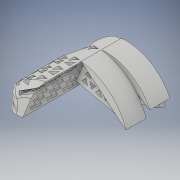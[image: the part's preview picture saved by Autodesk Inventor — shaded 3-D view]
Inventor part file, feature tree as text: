
AUTODESK INVENTOR PART (.ipt)
format: ipt  version: 2017 (Build 210142000, 142)  size: 1,097,728 bytes
history: native  units: mm
features: sketch x28, extrude x24, plane x7, fillet x6, other x3, boolean_combine x1, revolve x1, sweep x1
ambient origin geometry x8: Origin, YZ Plane, XZ Plane, XY Plane, X Axis, Y Axis, Z Axis, Center Point
bodies: Solid1 (feature_tree), Solid2 (feature_tree), Solid3 (feature_tree), Solid4 (feature_tree), Solid5 (feature_tree)
feature tree (71):
  extrude  "Extrusion1"  Depth=35.0mm
  plane  "Work Plane1"
  extrude  "Extrusion2"  Depth=33.005mm
  extrude  "Extrusion3"  TaperAngle=0.0deg  [1 undecoded]
  plane  "Work Plane2"
  extrude  "Extrusion4"  Depth=20.0mm
  other  "Work Axis1"
  extrude  "Extrusion5"  Depth=10.0mm
  sketch  "Sketch6"  dims[d12=48.556624mm d13=20.0mm d14=0.0mm]
  boolean_combine  "Combine1"
  extrude  "Extrusion6"  Depth=20.0mm TaperAngle=0.0deg
  extrude  "Extrusion7"  Depth=53.287466mm TaperAngle=0.0deg
  other  "Work Axis2"
  fillet  "Fillet1"  Radius=53.287466mm
  revolve  "Revolution1"  [1 undecoded]
  extrude  "Extrusion8"  Depth=61.358233mm
  sketch  "Sketch10"  dims[d25=7.433428mm d26=13.25mm d27=0.0mm]
  plane  "Work Plane3"
  sweep  "Sweep1"
  extrude  "Extrusion9"  TaperAngle=90.0deg  [1 undecoded]
  fillet  "Fillet2"  Radius=40.197898mm
  extrude  "Extrusion10"  Depth=15.060899mm
  extrude  "Extrusion11"  Depth=10.650813mm
  extrude  "Extrusion12"  Depth=5.3475mm
  fillet  "Fillet3"  Radius=15.0mm
  fillet  "Fillet4"  [1 undecoded]
  fillet  "Fillet5"  Radius=27.295196mm
  other  "Bend Part1"
  extrude  "Extrusion13"  Depth=5.348mm
  plane  "Work Plane4"
  extrude  "Extrusion14"  TaperAngle=0.0deg  [1 undecoded]
  fillet  "Fillet6"  Radius=13.25mm
  extrude  "Extrusion15"  Depth=10.0mm TaperAngle=0.0deg
  plane  "Work Plane5"
  extrude  "Extrusion16"  Depth=10.0mm
  extrude  "Extrusion22"  Depth=10.0mm TaperAngle=0.0deg
  extrude  "Extrusion23"  Depth=10.0mm
  extrude  "Extrusion24"  Depth=10.0mm TaperAngle=180.0deg
  extrude  "Extrusion25"  Depth=18.153275mm
  plane  "Work Plane7"
  extrude  "Extrusion26"  TaperAngle=90.0deg  [1 undecoded]
  extrude  "Extrusion27"  Depth=57.396209mm
  extrude  "Extrusion28"  Depth=2.0mm
  plane  "Work Plane8"
  extrude  "Extrusion29"  Depth=17.5mm
  sketch  "Sketch1"  dims[d0=60.0mm d1=35.0mm]
  sketch  "Sketch2"  dims[d2=60.0mm d3=33.005mm]
  sketch  "Sketch3"  dims[d4=75.0mm d5=0.0mm d6=0.0mm]
  sketch  "Sketch4"  dims[d7=35.0mm d8=20.0mm]
  sketch  "Sketch5"  dims[d9=55.0mm d10=0.0mm d11=10.0mm]
  sketch  "Sketch7"  dims[d15=90.0deg d16=20.0mm d17=0.0mm d18=53.287466mm]
  sketch  "Sketch8"  dims[d19=20.0mm d20=0.0mm d21=14.476257mm]
  sketch  "Sketch9"  dims[d22=20.0mm d23=0.0mm d24=61.358233mm]
  sketch  "Sketch11"  dims[d28=10.0mm d29=90.0deg d30=40.197898mm]
  sketch  "Sketch12"  dims[d31=90.965929mm d32=15.060899mm]
  sketch  "Sketch13"  dims[d33=0.0mm d34=0.0mm d35=10.650813mm]
  sketch  "Sketch15"  dims[d36=90.0deg d37=5.3475mm d38=15.0mm d39=45.0deg d40=27.295196mm]
  sketch  "Sketch16"  dims[d41=20.0mm d42=5.348mm]
  sketch  "Sketch18"  dims[d43=60.0mm d44=0.0mm d45=0.0mm d46=13.25mm d47=0.0mm]
  sketch  "Sketch19"  dims[d48=10.0mm d49=75.0mm d50=0.0mm]
  sketch  "Sketch20"  dims[d52=10.0mm d53=10.80569mm]
  sketch  "Sketch21"  dims[d54=10.0mm d55=0.0mm d56=4.8mm d57=0.0mm]
  sketch  "Sketch22"  dims[d58=10.0mm d59=10.0mm]
  sketch  "Sketch28"  dims[d60=10.0mm d62=2.0mm d63=180.0deg]
  sketch  "Sketch29"  dims[d64=18.153275mm d65=18.153275mm]
  sketch  "Sketch30"  dims[d66=75.0mm d67=0.0mm d68=90.0deg]
  sketch  "Sketch31"  dims[d69=75.0mm d70=57.396209mm]
  sketch  "Sketch32"  dims[d71=75.0mm d72=0.0mm d73=2.0mm]
  sketch  "Sketch33"  dims[d74=27.7545mm d75=17.5mm]
  sketch  "Sketch34"  dims[d76=5.0mm d77=0.0mm]
  sketch  "Sketch35"  dims[d78=20.0mm d79=28.8585mm d80=10.0mm d81=0.0mm d108=10.0mm d109=0.0mm d110=5.0mm d111=0.0mm d112=20.0mm d113=3.0mm d114=2.5mm d115=19.198622mm d116=10.0mm d117=0.0mm d118=20.0mm d119=3.0mm d120=13.189mm d121=20.0mm d122=3.0mm d123=11.073mm d124=10.0mm d125=5.0mm d126=0.0mm d127=0.0mm d128=5.202827mm d129=2.5mm d130=20.0mm d131=47.662mm d132=0.0mm d133=6.0mm d134=4.0mm d136=4.0mm d137=6.0mm d138=4.0mm d140=4.0mm d141=30.0mm d143=16.0mm d144=30.0mm d146=8.0mm d149=20.0mm d151=19.0mm d152=10.0mm d154=10.0mm d156=20.0mm d158=8.0mm d159=10.0mm d161=10.0mm d163=0.0mm d164=0.0mm d165=6.0mm d166=4.0mm d167=4.0mm d168=6.0mm d169=4.0mm d170=4.0mm d171=20.0mm d173=14.0mm d174=20.0mm d176=8.0mm d179=10.0mm d180=0.0mm d181=10.0mm d182=6.0mm d183=4.0mm d185=4.0mm d186=6.0mm d187=4.0mm d188=4.0mm d189=40.0mm d191=14.0mm d192=10.0mm d194=10.0mm d196=20.0mm d198=12.0mm d199=10.0mm d201=10.0mm d203=20.0mm d205=8.0mm d206=10.0mm d208=10.0mm d210=20.0mm d211=0.0mm]
note: 6 required parameter values undecoded (feature->parameter linkage not recoverable at this tier; creation-order binding heuristic only, values carry confidence <= 0.55)